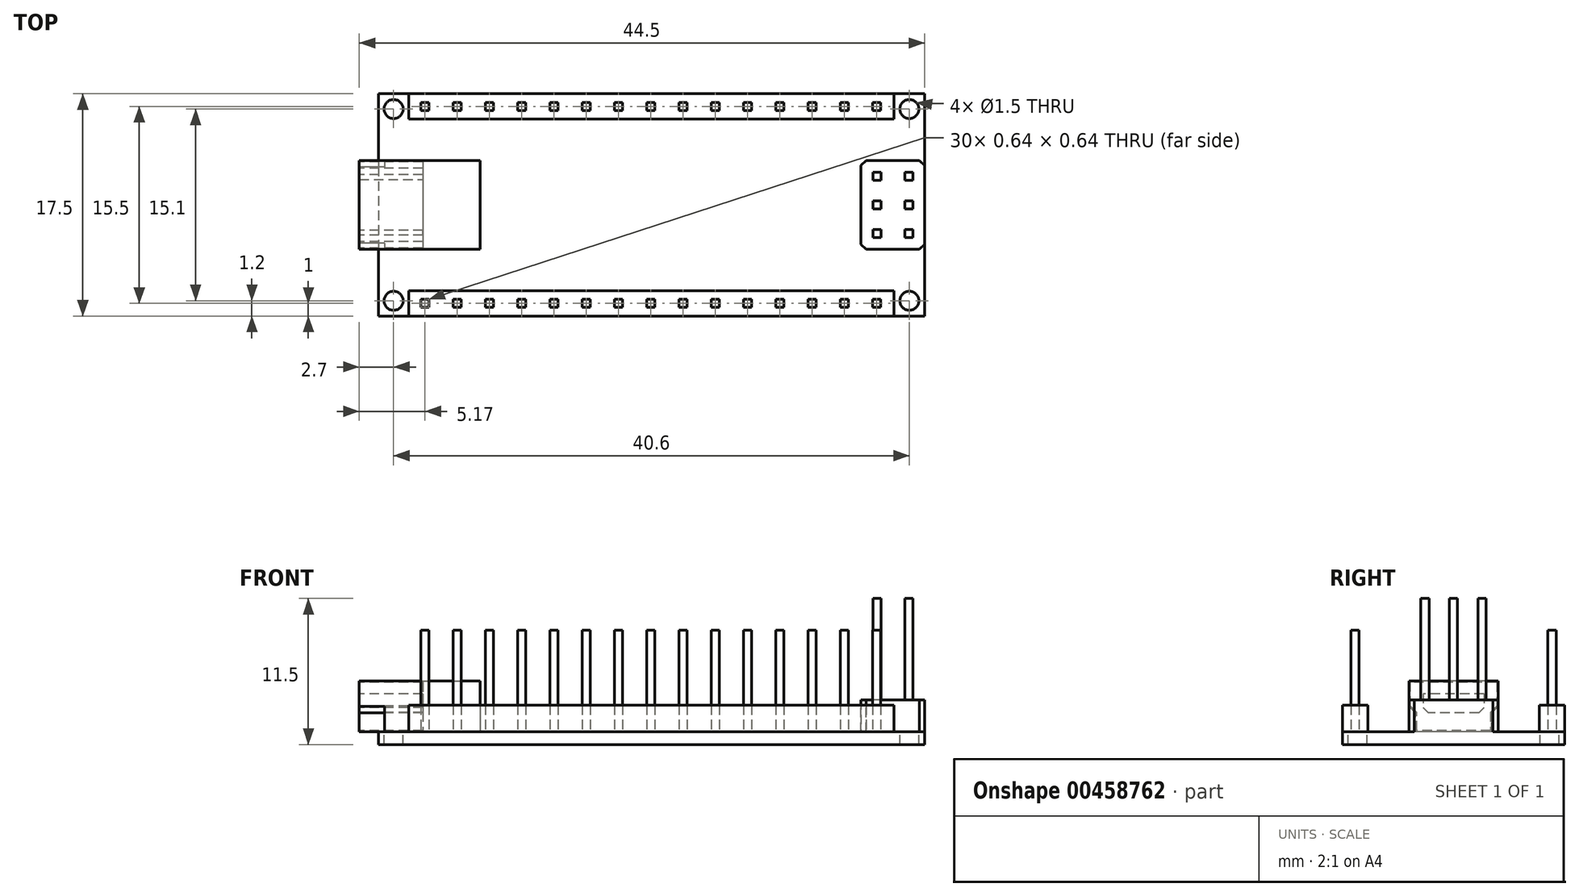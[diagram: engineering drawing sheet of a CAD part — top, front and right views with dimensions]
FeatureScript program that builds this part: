
annotation { "Feature Type Name" : "Feature", "Feature Type Description" : "" }
export const myFeature = defineFeature(function(context is Context, id is Id, definition is map)
    precondition{}
    {
        {
            var Q0;
            Q0=qCreatedBy(makeId("Top.planeOp"),FACE);
            var sketch = newSketch(context, id + "F0", { "sketchPlane" : qUnion([Q0])});
            skLineSegment(sketch, "E0.bottom", {"start": v(21.5, 8.75) * mm, "end": v(-21.5, 8.75) * mm});
            skLineSegment(sketch, "E0.top", {"start": v(21.5, -8.75) * mm, "end": v(-21.5, -8.75) * mm});
            skLineSegment(sketch, "E0.left", {"start": v(21.5, 8.75) * mm, "end": v(21.5, -8.75) * mm});
            skLineSegment(sketch, "E0.right", {"start": v(-21.5, 8.75) * mm, "end": v(-21.5, -8.75) * mm});
            skPoint(sketch, "E0.middle", {"position": v(0, 0) * mm});
            skCircle(sketch, "E1", {"center": v(-20.3, 7.55) * mm, "radius": 0.75 * mm});
            skCircle(sketch, "E2.0.1.0", {"center": v(-20.3, -7.55) * mm, "radius": 0.75 * mm});
            skCircle(sketch, "E2.1.0.0", {"center": v(20.3, 7.55) * mm, "radius": 0.75 * mm});
            skCircle(sketch, "E2.1.1.0", {"center": v(20.3, -7.55) * mm, "radius": 0.75 * mm});
            skLineSegment(sketch, "E2.direction1", {"start": v(-20.3, 7.55) * mm, "end": v(20.3, 7.55) * mm, "construction": true});
            skLineSegment(sketch, "E2.direction2", {"start": v(-20.3, 7.55) * mm, "end": v(-20.3, -7.55) * mm, "construction": true});
            skPoint(sketch, "E3", {"position": v(21.5, 0) * mm});
            skPoint(sketch, "E4", {"position": v(-21.5, 0) * mm});
            skLineSegment(sketch, "E5.bottom", {"start": v(-23, 3.5) * mm, "end": v(-13.5, 3.5) * mm});
            skLineSegment(sketch, "E5.top", {"start": v(-23, -3.5) * mm, "end": v(-13.5, -3.5) * mm});
            skLineSegment(sketch, "E5.left", {"start": v(-23, 3.5) * mm, "end": v(-23, -3.5) * mm});
            skLineSegment(sketch, "E5.right", {"start": v(-13.5, 3.5) * mm, "end": v(-13.5, -3.5) * mm});
            skPoint(sketch, "E6", {"position": v(-13.5, 0) * mm});
            skLineSegment(sketch, "E7.bottom", {"start": v(21.5, 3.5) * mm, "end": v(16.5, 3.5) * mm});
            skLineSegment(sketch, "E7.top", {"start": v(21.5, -3.5) * mm, "end": v(16.5, -3.5) * mm});
            skLineSegment(sketch, "E7.left", {"start": v(21.5, 3.5) * mm, "end": v(21.5, -3.5) * mm});
            skLineSegment(sketch, "E7.right", {"start": v(16.5, 3.5) * mm, "end": v(16.5, -3.5) * mm});
            skSolve(sketch);
        }
        {
            var Q0;
            {var subQ5=sQuery(id+"F0.wireOp",EDGE,"E5.right");Q0=makeQuery(id+"F0.imprint","IMPRINT",FACE,{"disambiguationData":[TD([[makeQuery(id+"F0.imprint","IMPRINT",EDGE,{"derivedFrom":subQ5}),-1.0]])]});}
            var Q1;
            {var subQ0=sQuery(id+"F0.wireOp",EDGE,"E0.bottom");Q1=makeQuery(id+"F0.imprint","IMPRINT",FACE,{"disambiguationData":[TD([[makeQuery(id+"F0.imprint","IMPRINT",EDGE,{"derivedFrom":subQ0}),1.0]])]});}
            var Q2;
            Q2=makeQuery(id+"F0.imprint","IMPRINT",FACE,{"disambiguationData":[TD([[makeQuery(id+"F0.imprint","IMPRINT",EDGE,{"derivedFrom":sQuery(id+"F0.wireOp",EDGE,"E7.bottom")}),1.0]])]});
            extrude(context, id + "F1", {"entities" : qUnion([Q0, Q1, Q2]), "oppositeDirection" : true, "depth" : 1 * mm});
        }
        {
            var Q0;
            {var subQ5=sQuery(id+"F0.wireOp",EDGE,"E5.left");Q0=makeQuery(id+"F0.imprint","IMPRINT",FACE,{"disambiguationData":[TD([[makeQuery(id+"F0.imprint","IMPRINT",EDGE,{"derivedFrom":subQ5}),1.0]])]});}
            var Q1;
            {var subQ5=sQuery(id+"F0.wireOp",EDGE,"E5.right");Q1=makeQuery(id+"F0.imprint","IMPRINT",FACE,{"disambiguationData":[TD([[makeQuery(id+"F0.imprint","IMPRINT",EDGE,{"derivedFrom":subQ5}),-1.0]])]});}
            extrude(context, id + "F2", {"entities" : qUnion([Q0, Q1]), "operationType" : NewBodyOperationType.ADD, "depth" : 4 * mm});
        }
        {
            var Q0;
            Q0=makeQuery(id+"F0.imprint","IMPRINT",FACE,{"disambiguationData":[TD([[makeQuery(id+"F0.imprint","IMPRINT",EDGE,{"derivedFrom":sQuery(id+"F0.wireOp",EDGE,"E7.bottom")}),1.0]])]});
            extrude(context, id + "F3", {"entities" : qUnion([Q0]), "operationType" : NewBodyOperationType.ADD, "depth" : 2.5 * mm});
        }
        {
            var Q0;
            Q0=makeQuery(id+"F2.opExtrude","SWEPT_FACE",FACE,{"disambiguationData":[OSD([sQuery(id+"F0.wireOp",EDGE,"E5.left")])]});
            var sketch = newSketch(context, id + "F4", { "sketchPlane" : qUnion([Q0])});
            skPoint(sketch, "E8", {"position": v(-3.5, 2) * mm});
            skPoint(sketch, "E9", {"position": v(3.5, 2) * mm});
            skPoint(sketch, "E10", {"position": v(-3, 0) * mm});
            skPoint(sketch, "E11", {"position": v(3, 0) * mm});
            skPoint(sketch, "E12", {"position": v(-3, 1.5) * mm});
            skPoint(sketch, "E13", {"position": v(3, 1.5) * mm});
            skLineSegment(sketch, "E14", {"start": v(-3.5, 2) * mm, "end": v(-3, 1.5) * mm});
            skLineSegment(sketch, "E15", {"start": v(-3, 0) * mm, "end": v(-3, 1.5) * mm});
            skLineSegment(sketch, "E16", {"start": v(3, 0) * mm, "end": v(3, 1.5) * mm});
            skLineSegment(sketch, "E17", {"start": v(3, 1.5) * mm, "end": v(3.5, 2) * mm});
            skLineSegment(sketch, "E18.bottom", {"start": v(-2.4, 3) * mm, "end": v(2.4, 3) * mm});
            skLineSegment(sketch, "E18.top", {"start": v(-2.4, 1.5) * mm, "end": v(2.4, 1.5) * mm});
            skLineSegment(sketch, "E18.left", {"start": v(-2.4, 3) * mm, "end": v(-2.4, 1.5) * mm});
            skLineSegment(sketch, "E18.right", {"start": v(2.4, 3) * mm, "end": v(2.4, 1.5) * mm});
            skPoint(sketch, "E19", {"position": v(0, 3) * mm});
            skPoint(sketch, "E20", {"position": v(-2.4, 2.25) * mm});
            skPoint(sketch, "E21", {"position": v(-3.5, 4) * mm});
            skPoint(sketch, "E22", {"position": v(3.5, 4) * mm});
            skLineSegment(sketch, "E23.0", {"start": v(-3.5, -1) * mm, "end": v(3.5, -1) * mm});
            skLineSegment(sketch, "E24", {"start": v(-3.5, 4) * mm, "end": v(-3.5, 2) * mm});
            skLineSegment(sketch, "E25", {"start": v(-3, 1.5) * mm, "end": v(-3, 0) * mm});
            skLineSegment(sketch, "E26", {"start": v(-3, 0) * mm, "end": v(3, 0) * mm});
            skLineSegment(sketch, "E27", {"start": v(3.5, 2) * mm, "end": v(3.5, 4) * mm});
            skLineSegment(sketch, "E28.0", {"start": v(-3.4, 3.9) * mm, "end": v(3.4, 3.9) * mm});
            skLineSegment(sketch, "E28.1", {"start": v(3.4, 2.04) * mm, "end": v(3.4, 3.9) * mm});
            skLineSegment(sketch, "E28.2", {"start": v(-3.4, 3.9) * mm, "end": v(-3.4, 2.04) * mm});
            skLineSegment(sketch, "E28.3", {"start": v(2.9, 1.54) * mm, "end": v(3.4, 2.04) * mm});
            skLineSegment(sketch, "E28.4", {"start": v(-3.4, 2.04) * mm, "end": v(-2.9, 1.54) * mm});
            skLineSegment(sketch, "E28.5", {"start": v(-2.9, 1.54) * mm, "end": v(-2.9, 0.1) * mm});
            skLineSegment(sketch, "E28.6", {"start": v(-2.9, 0.1) * mm, "end": v(2.9, 0.1) * mm});
            skLineSegment(sketch, "E28.7", {"start": v(2.9, 0.1) * mm, "end": v(2.9, 1.54) * mm});
            skPoint(sketch, "E29", {"position": v(-3.4, 2.04) * mm});
            skPoint(sketch, "E30", {"position": v(-2.9, 1.54) * mm});
            skSolve(sketch);
        }
        {
            var Q0;
            Q0=makeQuery(id+"F4.imprint","IMPRINT",FACE,{"disambiguationData":[TD([[makeQuery(id+"F4.imprint","IMPRINT",EDGE,{"derivedFrom":sQuery(id+"F4.wireOp",EDGE,"E18.bottom")}),1.0]])]});
            extrude(context, id + "F5", {"entities" : qUnion([Q0]), "operationType" : NewBodyOperationType.REMOVE, "oppositeDirection" : true, "depth" : 5 * mm});
        }
        {
            var Q0;
            {var subQ0=sQuery(id+"F4.wireOp",EDGE,"E14");Q0=makeQuery(id+"F4.imprint","IMPRINT",FACE,{"disambiguationData":[TD([[makeQuery(id+"F4.imprint","IMPRINT",EDGE,{"derivedFrom":subQ0}),-1.0]])]});}
            var Q1;
            {var subQ0=sQuery(id+"F4.wireOp",EDGE,"E16");Q1=makeQuery(id+"F4.imprint","IMPRINT",FACE,{"disambiguationData":[TD([[makeQuery(id+"F4.imprint","IMPRINT",EDGE,{"derivedFrom":subQ0}),-1.0]])]});}
            extrude(context, id + "F6", {"entities" : qUnion([Q0, Q1]), "operationType" : NewBodyOperationType.REMOVE, "oppositeDirection" : true, "depth" : 2 * mm});
        }
        {
            var Q0;
            Q0=makeQuery(id+"F1.opExtrude","CAP_FACE",FACE,{"disambiguationData":[OSD([sQuery(id+"F0.wireOp",EDGE,"E0.bottom"),sQuery(id+"F0.wireOp",EDGE,"E0.top"),sQuery(id+"F0.wireOp",EDGE,"E0.left"),sQuery(id+"F0.wireOp",EDGE,"E0.right"),sQuery(id+"F0.wireOp",EDGE,"E1"),sQuery(id+"F0.wireOp",EDGE,"E2.0.1.0"),sQuery(id+"F0.wireOp",EDGE,"E2.1.0.0"),sQuery(id+"F0.wireOp",EDGE,"E2.1.1.0"),sQuery(id+"F0.wireOp",EDGE,"E7.left")])],"isStart":false});
            var sketch = newSketch(context, id + "F7", { "sketchPlane" : qUnion([Q0])});
            skLineSegment(sketch, "E31.bottom", {"start": v(-19.1, 8.75) * mm, "end": v(19.1, 8.75) * mm});
            skLineSegment(sketch, "E31.top", {"start": v(-19.1, 6.75) * mm, "end": v(19.1, 6.75) * mm});
            skLineSegment(sketch, "E31.left", {"start": v(-19.1, 8.75) * mm, "end": v(-19.1, 6.75) * mm});
            skLineSegment(sketch, "E31.right", {"start": v(19.1, 8.75) * mm, "end": v(19.1, 6.75) * mm});
            skPoint(sketch, "E32", {"position": v(0, 6.75) * mm});
            skLineSegment(sketch, "E33", {"start": v(-19.1, 7.75) * mm, "end": v(19.1, 7.75) * mm, "construction": true});
            skPoint(sketch, "E34", {"position": v(-17.83, 7.75) * mm});
            skLineSegment(sketch, "E35.bottom", {"start": v(-17.51, 8.07) * mm, "end": v(-18.15, 8.07) * mm});
            skLineSegment(sketch, "E35.top", {"start": v(-17.51, 7.43) * mm, "end": v(-18.15, 7.43) * mm});
            skLineSegment(sketch, "E35.left", {"start": v(-17.51, 8.07) * mm, "end": v(-17.51, 7.43) * mm});
            skLineSegment(sketch, "E35.right", {"start": v(-18.15, 8.07) * mm, "end": v(-18.15, 7.43) * mm});
            skPoint(sketch, "E36.1.0.0", {"position": v(-15.3, 7.75) * mm});
            skLineSegment(sketch, "E36.1.0.1", {"start": v(-14.97, 8.07) * mm, "end": v(-14.97, 7.43) * mm});
            skLineSegment(sketch, "E36.1.0.2", {"start": v(-14.97, 8.07) * mm, "end": v(-15.61, 8.07) * mm});
            skLineSegment(sketch, "E36.1.0.3", {"start": v(-15.61, 8.07) * mm, "end": v(-15.61, 7.43) * mm});
            skLineSegment(sketch, "E36.1.0.4", {"start": v(-14.97, 7.43) * mm, "end": v(-15.61, 7.43) * mm});
            skPoint(sketch, "E36.2.0.0", {"position": v(-12.75, 7.75) * mm});
            skLineSegment(sketch, "E36.2.0.1", {"start": v(-12.43, 8.07) * mm, "end": v(-12.43, 7.43) * mm});
            skLineSegment(sketch, "E36.2.0.2", {"start": v(-12.43, 8.07) * mm, "end": v(-13.07, 8.07) * mm});
            skLineSegment(sketch, "E36.2.0.3", {"start": v(-13.07, 8.07) * mm, "end": v(-13.07, 7.43) * mm});
            skLineSegment(sketch, "E36.2.0.4", {"start": v(-12.43, 7.43) * mm, "end": v(-13.07, 7.43) * mm});
            skPoint(sketch, "E36.3.0.0", {"position": v(-10.21, 7.75) * mm});
            skLineSegment(sketch, "E36.3.0.1", {"start": v(-9.89, 8.07) * mm, "end": v(-9.89, 7.43) * mm});
            skLineSegment(sketch, "E36.3.0.2", {"start": v(-9.89, 8.07) * mm, "end": v(-10.53, 8.07) * mm});
            skLineSegment(sketch, "E36.3.0.3", {"start": v(-10.53, 8.07) * mm, "end": v(-10.53, 7.43) * mm});
            skLineSegment(sketch, "E36.3.0.4", {"start": v(-9.89, 7.43) * mm, "end": v(-10.53, 7.43) * mm});
            skPoint(sketch, "E36.4.0.0", {"position": v(-7.67, 7.75) * mm});
            skLineSegment(sketch, "E36.4.0.1", {"start": v(-7.35, 8.07) * mm, "end": v(-7.35, 7.43) * mm});
            skLineSegment(sketch, "E36.4.0.2", {"start": v(-7.35, 8.07) * mm, "end": v(-8, 8.07) * mm});
            skLineSegment(sketch, "E36.4.0.3", {"start": v(-8, 8.07) * mm, "end": v(-8, 7.43) * mm});
            skLineSegment(sketch, "E36.4.0.4", {"start": v(-7.35, 7.43) * mm, "end": v(-8, 7.43) * mm});
            skPoint(sketch, "E36.5.0.0", {"position": v(-5.13, 7.75) * mm});
            skLineSegment(sketch, "E36.5.0.1", {"start": v(-4.8, 8.07) * mm, "end": v(-4.8, 7.43) * mm});
            skLineSegment(sketch, "E36.5.0.2", {"start": v(-4.8, 8.07) * mm, "end": v(-5.45, 8.07) * mm});
            skLineSegment(sketch, "E36.5.0.3", {"start": v(-5.45, 8.07) * mm, "end": v(-5.45, 7.43) * mm});
            skLineSegment(sketch, "E36.5.0.4", {"start": v(-4.8, 7.43) * mm, "end": v(-5.45, 7.43) * mm});
            skPoint(sketch, "E36.6.0.0", {"position": v(-2.59, 7.75) * mm});
            skLineSegment(sketch, "E36.6.0.1", {"start": v(-2.27, 8.07) * mm, "end": v(-2.27, 7.43) * mm});
            skLineSegment(sketch, "E36.6.0.2", {"start": v(-2.27, 8.07) * mm, "end": v(-2.9, 8.07) * mm});
            skLineSegment(sketch, "E36.6.0.3", {"start": v(-2.9, 8.07) * mm, "end": v(-2.9, 7.43) * mm});
            skLineSegment(sketch, "E36.6.0.4", {"start": v(-2.27, 7.43) * mm, "end": v(-2.9, 7.43) * mm});
            skPoint(sketch, "E36.7.0.0", {"position": v(-0.05, 7.75) * mm});
            skLineSegment(sketch, "E36.7.0.1", {"start": v(0.27, 8.07) * mm, "end": v(0.27, 7.43) * mm});
            skLineSegment(sketch, "E36.7.0.2", {"start": v(0.27, 8.07) * mm, "end": v(-0.37, 8.07) * mm});
            skLineSegment(sketch, "E36.7.0.3", {"start": v(-0.37, 8.07) * mm, "end": v(-0.37, 7.43) * mm});
            skLineSegment(sketch, "E36.7.0.4", {"start": v(0.27, 7.43) * mm, "end": v(-0.37, 7.43) * mm});
            skPoint(sketch, "E36.8.0.0", {"position": v(2.5, 7.75) * mm});
            skLineSegment(sketch, "E36.8.0.1", {"start": v(2.81, 8.07) * mm, "end": v(2.81, 7.43) * mm});
            skLineSegment(sketch, "E36.8.0.2", {"start": v(2.81, 8.07) * mm, "end": v(2.17, 8.07) * mm});
            skLineSegment(sketch, "E36.8.0.3", {"start": v(2.17, 8.07) * mm, "end": v(2.17, 7.43) * mm});
            skLineSegment(sketch, "E36.8.0.4", {"start": v(2.81, 7.43) * mm, "end": v(2.17, 7.43) * mm});
            skPoint(sketch, "E36.9.0.0", {"position": v(5.03, 7.75) * mm});
            skLineSegment(sketch, "E36.9.0.1", {"start": v(5.35, 8.07) * mm, "end": v(5.35, 7.43) * mm});
            skLineSegment(sketch, "E36.9.0.2", {"start": v(5.35, 8.07) * mm, "end": v(4.71, 8.07) * mm});
            skLineSegment(sketch, "E36.9.0.3", {"start": v(4.71, 8.07) * mm, "end": v(4.71, 7.43) * mm});
            skLineSegment(sketch, "E36.9.0.4", {"start": v(5.35, 7.43) * mm, "end": v(4.71, 7.43) * mm});
            skPoint(sketch, "E36.10.0.0", {"position": v(7.57, 7.75) * mm});
            skLineSegment(sketch, "E36.10.0.1", {"start": v(7.9, 8.07) * mm, "end": v(7.9, 7.43) * mm});
            skLineSegment(sketch, "E36.10.0.2", {"start": v(7.9, 8.07) * mm, "end": v(7.25, 8.07) * mm});
            skLineSegment(sketch, "E36.10.0.3", {"start": v(7.25, 8.07) * mm, "end": v(7.25, 7.43) * mm});
            skLineSegment(sketch, "E36.10.0.4", {"start": v(7.9, 7.43) * mm, "end": v(7.25, 7.43) * mm});
            skPoint(sketch, "E36.11.0.0", {"position": v(10.11, 7.75) * mm});
            skLineSegment(sketch, "E36.11.0.1", {"start": v(10.43, 8.07) * mm, "end": v(10.43, 7.43) * mm});
            skLineSegment(sketch, "E36.11.0.2", {"start": v(10.43, 8.07) * mm, "end": v(9.8, 8.07) * mm});
            skLineSegment(sketch, "E36.11.0.3", {"start": v(9.8, 8.07) * mm, "end": v(9.8, 7.43) * mm});
            skLineSegment(sketch, "E36.11.0.4", {"start": v(10.43, 7.43) * mm, "end": v(9.8, 7.43) * mm});
            skPoint(sketch, "E36.12.0.0", {"position": v(12.65, 7.75) * mm});
            skLineSegment(sketch, "E36.12.0.1", {"start": v(12.97, 8.07) * mm, "end": v(12.97, 7.43) * mm});
            skLineSegment(sketch, "E36.12.0.2", {"start": v(12.97, 8.07) * mm, "end": v(12.33, 8.07) * mm});
            skLineSegment(sketch, "E36.12.0.3", {"start": v(12.33, 8.07) * mm, "end": v(12.33, 7.43) * mm});
            skLineSegment(sketch, "E36.12.0.4", {"start": v(12.97, 7.43) * mm, "end": v(12.33, 7.43) * mm});
            skPoint(sketch, "E36.13.0.0", {"position": v(15.2, 7.75) * mm});
            skLineSegment(sketch, "E36.13.0.1", {"start": v(15.51, 8.07) * mm, "end": v(15.51, 7.43) * mm});
            skLineSegment(sketch, "E36.13.0.2", {"start": v(15.51, 8.07) * mm, "end": v(14.87, 8.07) * mm});
            skLineSegment(sketch, "E36.13.0.3", {"start": v(14.87, 8.07) * mm, "end": v(14.87, 7.43) * mm});
            skLineSegment(sketch, "E36.13.0.4", {"start": v(15.51, 7.43) * mm, "end": v(14.87, 7.43) * mm});
            skPoint(sketch, "E36.14.0.0", {"position": v(17.73, 7.75) * mm});
            skLineSegment(sketch, "E36.14.0.1", {"start": v(18.05, 8.07) * mm, "end": v(18.05, 7.43) * mm});
            skLineSegment(sketch, "E36.14.0.2", {"start": v(18.05, 8.07) * mm, "end": v(17.41, 8.07) * mm});
            skLineSegment(sketch, "E36.14.0.3", {"start": v(17.41, 8.07) * mm, "end": v(17.41, 7.43) * mm});
            skLineSegment(sketch, "E36.14.0.4", {"start": v(18.05, 7.43) * mm, "end": v(17.41, 7.43) * mm});
            skLineSegment(sketch, "E36.direction1", {"start": v(-17.83, 7.75) * mm, "end": v(-15.3, 7.75) * mm, "construction": true});
            skPoint(sketch, "E37", {"position": v(-20.3, 7.55) * mm});
            skLineSegment(sketch, "E38", {"start": v(-20.3, 7.55) * mm, "end": v(-21.5, 7.55) * mm});
            skLineSegment(sketch, "E39", {"start": v(-21.5, 7.55) * mm, "end": v(-19.1, 7.55) * mm});
            skPoint(sketch, "E40", {"position": v(-21.05, 7.55) * mm});
            skPoint(sketch, "E41", {"position": v(-19.55, 7.55) * mm});
            skPoint(sketch, "E42", {"position": v(20.3, 7.55) * mm});
            skLineSegment(sketch, "E43", {"start": v(20.3, 7.55) * mm, "end": v(21.5, 7.55) * mm});
            skLineSegment(sketch, "E44", {"start": v(21.5, 7.55) * mm, "end": v(19.1, 7.55) * mm});
            skPoint(sketch, "E45", {"position": v(21.05, 7.55) * mm});
            skPoint(sketch, "E46", {"position": v(19.55, 7.55) * mm});
            skPoint(sketch, "E47.0.1.0", {"position": v(-0.05, -7.75) * mm});
            skPoint(sketch, "E47.0.1.1", {"position": v(-5.13, -7.75) * mm});
            skPoint(sketch, "E47.0.1.2", {"position": v(12.65, -7.75) * mm});
            skPoint(sketch, "E47.0.1.3", {"position": v(-7.67, -7.75) * mm});
            skPoint(sketch, "E47.0.1.4", {"position": v(17.73, -7.75) * mm});
            skPoint(sketch, "E47.0.1.5", {"position": v(-10.21, -7.75) * mm});
            skPoint(sketch, "E47.0.1.6", {"position": v(7.57, -7.75) * mm});
            skPoint(sketch, "E47.0.1.7", {"position": v(2.49, -7.75) * mm});
            skPoint(sketch, "E47.0.1.8", {"position": v(0, -8.75) * mm});
            skPoint(sketch, "E47.0.1.9", {"position": v(-17.83, -7.75) * mm});
            skPoint(sketch, "E47.0.1.10", {"position": v(5.03, -7.75) * mm});
            skPoint(sketch, "E47.0.1.11", {"position": v(-15.3, -7.75) * mm});
            skLineSegment(sketch, "E47.0.1.12", {"start": v(-17.83, -7.75) * mm, "end": v(-15.3, -7.75) * mm, "construction": true});
            skPoint(sketch, "E47.0.1.13", {"position": v(10.11, -7.75) * mm});
            skPoint(sketch, "E47.0.1.14", {"position": v(15.2, -7.75) * mm});
            skPoint(sketch, "E47.0.1.15", {"position": v(-2.6, -7.75) * mm});
            skPoint(sketch, "E47.0.1.16", {"position": v(-12.75, -7.75) * mm});
            skPoint(sketch, "E47.0.1.17", {"position": v(-17.83, -7.75) * mm});
            skLineSegment(sketch, "E47.0.1.18", {"start": v(18.05, -7.43) * mm, "end": v(17.41, -7.43) * mm});
            skLineSegment(sketch, "E47.0.1.19", {"start": v(18.05, -8.07) * mm, "end": v(17.41, -8.07) * mm});
            skLineSegment(sketch, "E47.0.1.20", {"start": v(18.05, -7.43) * mm, "end": v(18.05, -8.07) * mm});
            skLineSegment(sketch, "E47.0.1.21", {"start": v(-0.37, -7.43) * mm, "end": v(-0.37, -8.07) * mm});
            skLineSegment(sketch, "E47.0.1.22", {"start": v(-10.53, -7.43) * mm, "end": v(-10.53, -8.07) * mm});
            skLineSegment(sketch, "E47.0.1.23", {"start": v(-9.89, -7.43) * mm, "end": v(-10.53, -7.43) * mm});
            skLineSegment(sketch, "E47.0.1.24", {"start": v(-2.27, -7.43) * mm, "end": v(-2.9, -7.43) * mm});
            skLineSegment(sketch, "E47.0.1.25", {"start": v(12.97, -7.43) * mm, "end": v(12.97, -8.07) * mm});
            skLineSegment(sketch, "E47.0.1.26", {"start": v(-5.45, -7.43) * mm, "end": v(-5.45, -8.07) * mm});
            skLineSegment(sketch, "E47.0.1.27", {"start": v(-7.35, -8.07) * mm, "end": v(-7.99, -8.07) * mm});
            skLineSegment(sketch, "E47.0.1.28", {"start": v(2.81, -8.07) * mm, "end": v(2.17, -8.07) * mm});
            skLineSegment(sketch, "E47.0.1.29", {"start": v(12.97, -8.07) * mm, "end": v(12.33, -8.07) * mm});
            skLineSegment(sketch, "E47.0.1.30", {"start": v(7.9, -8.07) * mm, "end": v(7.25, -8.07) * mm});
            skLineSegment(sketch, "E47.0.1.31", {"start": v(7.25, -7.43) * mm, "end": v(7.25, -8.07) * mm});
            skLineSegment(sketch, "E47.0.1.32", {"start": v(-2.9, -7.43) * mm, "end": v(-2.9, -8.07) * mm});
            skLineSegment(sketch, "E47.0.1.33", {"start": v(-7.35, -7.43) * mm, "end": v(-7.99, -7.43) * mm});
            skLineSegment(sketch, "E47.0.1.34", {"start": v(2.81, -7.43) * mm, "end": v(2.81, -8.07) * mm});
            skLineSegment(sketch, "E47.0.1.35", {"start": v(7.9, -7.43) * mm, "end": v(7.25, -7.43) * mm});
            skLineSegment(sketch, "E47.0.1.36", {"start": v(-4.8, -8.07) * mm, "end": v(-5.45, -8.07) * mm});
            skLineSegment(sketch, "E47.0.1.37", {"start": v(-7.35, -7.43) * mm, "end": v(-7.35, -8.07) * mm});
            skLineSegment(sketch, "E47.0.1.38", {"start": v(15.5, -8.07) * mm, "end": v(14.87, -8.07) * mm});
            skLineSegment(sketch, "E47.0.1.39", {"start": v(5.35, -8.07) * mm, "end": v(4.71, -8.07) * mm});
            skLineSegment(sketch, "E47.0.1.40", {"start": v(-2.27, -8.07) * mm, "end": v(-2.9, -8.07) * mm});
            skLineSegment(sketch, "E47.0.1.41", {"start": v(-12.43, -8.07) * mm, "end": v(-13.07, -8.07) * mm});
            skLineSegment(sketch, "E47.0.1.42", {"start": v(2.81, -7.43) * mm, "end": v(2.17, -7.43) * mm});
            skLineSegment(sketch, "E47.0.1.43", {"start": v(17.41, -7.43) * mm, "end": v(17.41, -8.07) * mm});
            skLineSegment(sketch, "E47.0.1.44", {"start": v(12.97, -7.43) * mm, "end": v(12.33, -7.43) * mm});
            skLineSegment(sketch, "E47.0.1.45", {"start": v(7.9, -7.43) * mm, "end": v(7.9, -8.07) * mm});
            skLineSegment(sketch, "E47.0.1.46", {"start": v(-2.27, -7.43) * mm, "end": v(-2.27, -8.07) * mm});
            skLineSegment(sketch, "E47.0.1.47", {"start": v(-17.5, -8.07) * mm, "end": v(-18.15, -8.07) * mm});
            skLineSegment(sketch, "E47.0.1.48", {"start": v(12.33, -7.43) * mm, "end": v(12.33, -8.07) * mm});
            skLineSegment(sketch, "E47.0.1.49", {"start": v(-14.97, -7.43) * mm, "end": v(-14.97, -8.07) * mm});
            skLineSegment(sketch, "E47.0.1.50", {"start": v(2.17, -7.43) * mm, "end": v(2.17, -8.07) * mm});
            skLineSegment(sketch, "E47.0.1.51", {"start": v(-8, -7.43) * mm, "end": v(-8, -8.07) * mm});
            skLineSegment(sketch, "E47.0.1.52", {"start": v(-14.97, -7.43) * mm, "end": v(-15.6, -7.43) * mm});
            skLineSegment(sketch, "E47.0.1.53", {"start": v(-15.61, -7.43) * mm, "end": v(-15.61, -8.07) * mm});
            skLineSegment(sketch, "E47.0.1.54", {"start": v(-14.97, -8.07) * mm, "end": v(-15.6, -8.07) * mm});
            skLineSegment(sketch, "E47.0.1.55", {"start": v(-9.89, -7.43) * mm, "end": v(-9.89, -8.07) * mm});
            skLineSegment(sketch, "E47.0.1.56", {"start": v(0.27, -7.43) * mm, "end": v(0.27, -8.07) * mm});
            skLineSegment(sketch, "E47.0.1.57", {"start": v(10.43, -7.43) * mm, "end": v(10.43, -8.07) * mm});
            skLineSegment(sketch, "E47.0.1.58", {"start": v(-12.43, -7.43) * mm, "end": v(-12.43, -8.07) * mm});
            skLineSegment(sketch, "E47.0.1.59", {"start": v(10.43, -7.43) * mm, "end": v(9.8, -7.43) * mm});
            skLineSegment(sketch, "E47.0.1.60", {"start": v(0.27, -7.43) * mm, "end": v(-0.37, -7.43) * mm});
            skLineSegment(sketch, "E47.0.1.61", {"start": v(15.51, -7.43) * mm, "end": v(15.51, -8.07) * mm});
            skLineSegment(sketch, "E47.0.1.62", {"start": v(5.35, -7.43) * mm, "end": v(5.35, -8.07) * mm});
            skLineSegment(sketch, "E47.0.1.63", {"start": v(-4.8, -7.43) * mm, "end": v(-4.8, -8.07) * mm});
            skLineSegment(sketch, "E47.0.1.64", {"start": v(15.51, -7.43) * mm, "end": v(14.87, -7.43) * mm});
            skLineSegment(sketch, "E47.0.1.65", {"start": v(5.35, -7.43) * mm, "end": v(4.71, -7.43) * mm});
            skLineSegment(sketch, "E47.0.1.66", {"start": v(-4.8, -7.43) * mm, "end": v(-5.45, -7.43) * mm});
            skLineSegment(sketch, "E47.0.1.67", {"start": v(10.43, -8.07) * mm, "end": v(9.8, -8.07) * mm});
            skLineSegment(sketch, "E47.0.1.68", {"start": v(0.27, -8.07) * mm, "end": v(-0.37, -8.07) * mm});
            skLineSegment(sketch, "E47.0.1.69", {"start": v(-9.9, -8.07) * mm, "end": v(-10.53, -8.07) * mm});
            skLineSegment(sketch, "E47.0.1.70", {"start": v(4.71, -7.43) * mm, "end": v(4.71, -8.07) * mm});
            skLineSegment(sketch, "E47.0.1.71", {"start": v(14.87, -7.43) * mm, "end": v(14.87, -8.07) * mm});
            skLineSegment(sketch, "E47.0.1.72", {"start": v(9.8, -7.43) * mm, "end": v(9.8, -8.07) * mm});
            skLineSegment(sketch, "E47.0.1.73", {"start": v(-12.43, -7.43) * mm, "end": v(-13.07, -7.43) * mm});
            skLineSegment(sketch, "E47.0.1.74", {"start": v(-13.07, -7.43) * mm, "end": v(-13.07, -8.07) * mm});
            skLineSegment(sketch, "E47.0.1.75", {"start": v(-18.15, -7.43) * mm, "end": v(-18.15, -8.07) * mm});
            skLineSegment(sketch, "E47.0.1.76", {"start": v(-17.51, -7.43) * mm, "end": v(-17.51, -8.07) * mm});
            skLineSegment(sketch, "E47.0.1.77", {"start": v(-17.5, -7.43) * mm, "end": v(-18.15, -7.43) * mm});
            skLineSegment(sketch, "E47.0.1.78", {"start": v(19.1, -6.75) * mm, "end": v(19.1, -8.75) * mm});
            skLineSegment(sketch, "E47.0.1.79", {"start": v(-19.1, -8.75) * mm, "end": v(19.1, -8.75) * mm});
            skLineSegment(sketch, "E47.0.1.80", {"start": v(-19.1, -6.75) * mm, "end": v(-19.1, -8.75) * mm});
            skLineSegment(sketch, "E47.0.1.81", {"start": v(-19.1, -6.75) * mm, "end": v(19.1, -6.75) * mm});
            skLineSegment(sketch, "E47.direction1", {"start": v(-0.05, 7.75) * mm, "end": v(24.95, 7.75) * mm, "construction": true});
            skLineSegment(sketch, "E47.direction2", {"start": v(-0.05, 7.75) * mm, "end": v(-0.05, -7.75) * mm, "construction": true});
            skSolve(sketch);
        }
        {
            var Q0;
            Q0=makeQuery(id+"F7.imprint","IMPRINT",FACE,{"disambiguationData":[TD([[makeQuery(id+"F7.imprint","IMPRINT",EDGE,{"derivedFrom":sQuery(id+"F7.wireOp",EDGE,"E47.0.1.18")}),-1.0]])]});
            var Q1;
            {var subQ1=sQuery(id+"F7.wireOp",EDGE,"E31.bottom");Q1=makeQuery(id+"F7.imprint","IMPRINT",FACE,{"disambiguationData":[TD([[makeQuery(id+"F7.imprint","IMPRINT",EDGE,{"derivedFrom":subQ1}),1.0]])]});}
            extrude(context, id + "F8", {"entities" : qUnion([Q0, Q1]), "depth" : 2.1 * mm});
        }
        {
            var Q0;
            Q0=makeQuery(id+"F7.imprint","IMPRINT",FACE,{"disambiguationData":[TD([[makeQuery(id+"F7.imprint","IMPRINT",EDGE,{"derivedFrom":sQuery(id+"F7.wireOp",EDGE,"E35.bottom")}),1.0]])]});
            var Q1;
            Q1=makeQuery(id+"F7.imprint","IMPRINT",FACE,{"disambiguationData":[TD([[makeQuery(id+"F7.imprint","IMPRINT",EDGE,{"derivedFrom":sQuery(id+"F7.wireOp",EDGE,"E36.1.0.1")}),-1.0]])]});
            var Q2;
            Q2=makeQuery(id+"F7.imprint","IMPRINT",FACE,{"disambiguationData":[TD([[makeQuery(id+"F7.imprint","IMPRINT",EDGE,{"derivedFrom":sQuery(id+"F7.wireOp",EDGE,"E36.2.0.1")}),-1.0]])]});
            var Q3;
            Q3=makeQuery(id+"F7.imprint","IMPRINT",FACE,{"disambiguationData":[TD([[makeQuery(id+"F7.imprint","IMPRINT",EDGE,{"derivedFrom":sQuery(id+"F7.wireOp",EDGE,"E36.3.0.1")}),-1.0]])]});
            var Q4;
            Q4=makeQuery(id+"F7.imprint","IMPRINT",FACE,{"disambiguationData":[TD([[makeQuery(id+"F7.imprint","IMPRINT",EDGE,{"derivedFrom":sQuery(id+"F7.wireOp",EDGE,"E36.4.0.1")}),-1.0]])]});
            var Q5;
            Q5=makeQuery(id+"F7.imprint","IMPRINT",FACE,{"disambiguationData":[TD([[makeQuery(id+"F7.imprint","IMPRINT",EDGE,{"derivedFrom":sQuery(id+"F7.wireOp",EDGE,"E36.5.0.1")}),-1.0]])]});
            var Q6;
            Q6=makeQuery(id+"F7.imprint","IMPRINT",FACE,{"disambiguationData":[TD([[makeQuery(id+"F7.imprint","IMPRINT",EDGE,{"derivedFrom":sQuery(id+"F7.wireOp",EDGE,"E36.6.0.1")}),-1.0]])]});
            var Q7;
            Q7=makeQuery(id+"F7.imprint","IMPRINT",FACE,{"disambiguationData":[TD([[makeQuery(id+"F7.imprint","IMPRINT",EDGE,{"derivedFrom":sQuery(id+"F7.wireOp",EDGE,"E36.7.0.1")}),-1.0]])]});
            var Q8;
            Q8=makeQuery(id+"F7.imprint","IMPRINT",FACE,{"disambiguationData":[TD([[makeQuery(id+"F7.imprint","IMPRINT",EDGE,{"derivedFrom":sQuery(id+"F7.wireOp",EDGE,"E36.8.0.1")}),-1.0]])]});
            var Q9;
            Q9=makeQuery(id+"F7.imprint","IMPRINT",FACE,{"disambiguationData":[TD([[makeQuery(id+"F7.imprint","IMPRINT",EDGE,{"derivedFrom":sQuery(id+"F7.wireOp",EDGE,"E36.9.0.1")}),-1.0]])]});
            var Q10;
            Q10=makeQuery(id+"F7.imprint","IMPRINT",FACE,{"disambiguationData":[TD([[makeQuery(id+"F7.imprint","IMPRINT",EDGE,{"derivedFrom":sQuery(id+"F7.wireOp",EDGE,"E36.10.0.1")}),-1.0]])]});
            var Q11;
            Q11=makeQuery(id+"F7.imprint","IMPRINT",FACE,{"disambiguationData":[TD([[makeQuery(id+"F7.imprint","IMPRINT",EDGE,{"derivedFrom":sQuery(id+"F7.wireOp",EDGE,"E36.11.0.1")}),-1.0]])]});
            var Q12;
            Q12=makeQuery(id+"F7.imprint","IMPRINT",FACE,{"disambiguationData":[TD([[makeQuery(id+"F7.imprint","IMPRINT",EDGE,{"derivedFrom":sQuery(id+"F7.wireOp",EDGE,"E36.12.0.1")}),-1.0]])]});
            var Q13;
            Q13=makeQuery(id+"F7.imprint","IMPRINT",FACE,{"disambiguationData":[TD([[makeQuery(id+"F7.imprint","IMPRINT",EDGE,{"derivedFrom":sQuery(id+"F7.wireOp",EDGE,"E36.13.0.1")}),-1.0]])]});
            var Q14;
            Q14=makeQuery(id+"F7.imprint","IMPRINT",FACE,{"disambiguationData":[TD([[makeQuery(id+"F7.imprint","IMPRINT",EDGE,{"derivedFrom":sQuery(id+"F7.wireOp",EDGE,"E36.14.0.1")}),-1.0]])]});
            var Q15;
            Q15=makeQuery(id+"F7.imprint","IMPRINT",FACE,{"disambiguationData":[TD([[makeQuery(id+"F7.imprint","IMPRINT",EDGE,{"derivedFrom":sQuery(id+"F7.wireOp",EDGE,"E47.0.1.47")}),-1.0]])]});
            var Q16;
            Q16=makeQuery(id+"F7.imprint","IMPRINT",FACE,{"disambiguationData":[TD([[makeQuery(id+"F7.imprint","IMPRINT",EDGE,{"derivedFrom":sQuery(id+"F7.wireOp",EDGE,"E47.0.1.49")}),-1.0]])]});
            var Q17;
            Q17=makeQuery(id+"F7.imprint","IMPRINT",FACE,{"disambiguationData":[TD([[makeQuery(id+"F7.imprint","IMPRINT",EDGE,{"derivedFrom":sQuery(id+"F7.wireOp",EDGE,"E47.0.1.41")}),-1.0]])]});
            var Q18;
            Q18=makeQuery(id+"F7.imprint","IMPRINT",FACE,{"disambiguationData":[TD([[makeQuery(id+"F7.imprint","IMPRINT",EDGE,{"derivedFrom":sQuery(id+"F7.wireOp",EDGE,"E47.0.1.22")}),1.0]])]});
            var Q19;
            Q19=makeQuery(id+"F7.imprint","IMPRINT",FACE,{"disambiguationData":[TD([[makeQuery(id+"F7.imprint","IMPRINT",EDGE,{"derivedFrom":sQuery(id+"F7.wireOp",EDGE,"E47.0.1.27")}),-1.0]])]});
            var Q20;
            Q20=makeQuery(id+"F7.imprint","IMPRINT",FACE,{"disambiguationData":[TD([[makeQuery(id+"F7.imprint","IMPRINT",EDGE,{"derivedFrom":sQuery(id+"F7.wireOp",EDGE,"E47.0.1.26")}),1.0]])]});
            var Q21;
            Q21=makeQuery(id+"F7.imprint","IMPRINT",FACE,{"disambiguationData":[TD([[makeQuery(id+"F7.imprint","IMPRINT",EDGE,{"derivedFrom":sQuery(id+"F7.wireOp",EDGE,"E47.0.1.24")}),1.0]])]});
            var Q22;
            Q22=makeQuery(id+"F7.imprint","IMPRINT",FACE,{"disambiguationData":[TD([[makeQuery(id+"F7.imprint","IMPRINT",EDGE,{"derivedFrom":sQuery(id+"F7.wireOp",EDGE,"E47.0.1.21")}),1.0]])]});
            var Q23;
            Q23=makeQuery(id+"F7.imprint","IMPRINT",FACE,{"disambiguationData":[TD([[makeQuery(id+"F7.imprint","IMPRINT",EDGE,{"derivedFrom":sQuery(id+"F7.wireOp",EDGE,"E47.0.1.28")}),-1.0]])]});
            var Q24;
            Q24=makeQuery(id+"F7.imprint","IMPRINT",FACE,{"disambiguationData":[TD([[makeQuery(id+"F7.imprint","IMPRINT",EDGE,{"derivedFrom":sQuery(id+"F7.wireOp",EDGE,"E47.0.1.39")}),-1.0]])]});
            var Q25;
            Q25=makeQuery(id+"F7.imprint","IMPRINT",FACE,{"disambiguationData":[TD([[makeQuery(id+"F7.imprint","IMPRINT",EDGE,{"derivedFrom":sQuery(id+"F7.wireOp",EDGE,"E47.0.1.30")}),-1.0]])]});
            var Q26;
            Q26=makeQuery(id+"F7.imprint","IMPRINT",FACE,{"disambiguationData":[TD([[makeQuery(id+"F7.imprint","IMPRINT",EDGE,{"derivedFrom":sQuery(id+"F7.wireOp",EDGE,"E47.0.1.57")}),-1.0]])]});
            var Q27;
            Q27=makeQuery(id+"F7.imprint","IMPRINT",FACE,{"disambiguationData":[TD([[makeQuery(id+"F7.imprint","IMPRINT",EDGE,{"derivedFrom":sQuery(id+"F7.wireOp",EDGE,"E47.0.1.25")}),-1.0]])]});
            var Q28;
            Q28=makeQuery(id+"F7.imprint","IMPRINT",FACE,{"disambiguationData":[TD([[makeQuery(id+"F7.imprint","IMPRINT",EDGE,{"derivedFrom":sQuery(id+"F7.wireOp",EDGE,"E47.0.1.38")}),-1.0]])]});
            var Q29;
            Q29=makeQuery(id+"F7.imprint","IMPRINT",FACE,{"disambiguationData":[TD([[makeQuery(id+"F7.imprint","IMPRINT",EDGE,{"derivedFrom":sQuery(id+"F7.wireOp",EDGE,"E47.0.1.18")}),1.0]])]});
            extrude(context, id + "F9", {"entities" : qUnion([Q0, Q1, Q2, Q3, Q4, Q5, Q6, Q7, Q8, Q9, Q10, Q11, Q12, Q13, Q14, Q15, Q16, Q17, Q18, Q19, Q20, Q21, Q22, Q23, Q24, Q25, Q26, Q27, Q28, Q29]), "depth" : 8 * mm, "offsetDistance" : 25 * mm});
        }
        {
            var Q0;
            Q0=makeQuery(id+"F5.boolean.opBoolean","COPY",EDGE,{"derivedFrom":makeQuery(id+"F5.opExtrude","SWEPT_EDGE",EDGE,{"disambiguationData":[OSD([sQuery(id+"F4.wireOp",EDGE,"E18.top"),sQuery(id+"F4.wireOp",EDGE,"E18.right")])]})});
            var Q1;
            Q1=makeQuery(id+"F5.boolean.opBoolean","COPY",EDGE,{"derivedFrom":makeQuery(id+"F5.opExtrude","SWEPT_EDGE",EDGE,{"disambiguationData":[OSD([sQuery(id+"F4.wireOp",EDGE,"E18.top"),sQuery(id+"F4.wireOp",EDGE,"E18.left")])]})});
            chamfer(context, id + "F10", {"entities" : qUnion([Q0, Q1]), "width" : 0.4 * mm, "tangentPropagation" : true});
        }
        {
            var Q0;
            Q0=makeQuery(id+"F3.opExtrude","CAP_FACE",FACE,{"disambiguationData":[OSD([sQuery(id+"F0.wireOp",EDGE,"E7.bottom"),sQuery(id+"F0.wireOp",EDGE,"E7.top"),sQuery(id+"F0.wireOp",EDGE,"E7.left"),sQuery(id+"F0.wireOp",EDGE,"E7.right")])],"isStart":false});
            var sketch = newSketch(context, id + "F11", { "sketchPlane" : qUnion([Q0])});
            skPoint(sketch, "E48", {"position": v(21.5, 1.17) * mm});
            skPoint(sketch, "E49", {"position": v(21.5, -1.17) * mm});
            skLineSegment(sketch, "E50", {"start": v(21.5, 3.5) * mm, "end": v(21.5, 1.17) * mm});
            skLineSegment(sketch, "E51", {"start": v(21.5, -1.17) * mm, "end": v(21.5, 1.17) * mm});
            skLineSegment(sketch, "E52", {"start": v(21.5, -1.17) * mm, "end": v(21.5, -3.5) * mm});
            skLineSegment(sketch, "E53", {"start": v(21.5, 1.17) * mm, "end": v(16.5, 1.17) * mm});
            skLineSegment(sketch, "E54", {"start": v(21.5, -1.17) * mm, "end": v(16.5, -1.17) * mm});
            skPoint(sketch, "E55", {"position": v(19, 3.5) * mm});
            skPoint(sketch, "E56", {"position": v(19, -3.5) * mm});
            skLineSegment(sketch, "E57", {"start": v(19, 3.5) * mm, "end": v(19, -3.5) * mm});
            skPoint(sketch, "E58", {"position": v(17.75, 2.25) * mm});
            skLineSegment(sketch, "E59", {"start": v(17.75, 2.25) * mm, "end": v(17.75, 3.5) * mm, "construction": true});
            skLineSegment(sketch, "E60", {"start": v(17.75, 2.25) * mm, "end": v(16.5, 2.25) * mm, "construction": true});
            skLineSegment(sketch, "E61", {"start": v(17.75, 2.25) * mm, "end": v(19, 2.25) * mm, "construction": true});
            skLineSegment(sketch, "E62", {"start": v(17.75, 2.25) * mm, "end": v(17.75, 1.17) * mm, "construction": true});
            skLineSegment(sketch, "E63.bottom", {"start": v(18.07, 2.57) * mm, "end": v(17.43, 2.57) * mm});
            skLineSegment(sketch, "E63.top", {"start": v(18.07, 1.93) * mm, "end": v(17.43, 1.93) * mm});
            skLineSegment(sketch, "E63.left", {"start": v(18.07, 2.57) * mm, "end": v(18.07, 1.93) * mm});
            skLineSegment(sketch, "E63.right", {"start": v(17.43, 2.57) * mm, "end": v(17.43, 1.93) * mm});
            skLineSegment(sketch, "E64.1.0.0", {"start": v(20.57, 2.57) * mm, "end": v(20.57, 1.93) * mm});
            skLineSegment(sketch, "E64.1.0.1", {"start": v(20.57, 2.57) * mm, "end": v(19.93, 2.57) * mm});
            skLineSegment(sketch, "E64.1.0.2", {"start": v(19.93, 2.57) * mm, "end": v(19.93, 1.93) * mm});
            skLineSegment(sketch, "E64.1.0.3", {"start": v(20.57, 1.93) * mm, "end": v(19.93, 1.93) * mm});
            skPoint(sketch, "E65", {"position": v(20.25, 2.25) * mm});
            skLineSegment(sketch, "E66", {"start": v(19, 2.25) * mm, "end": v(20.25, 2.25) * mm, "construction": true});
            skLineSegment(sketch, "E67", {"start": v(20.25, 2.25) * mm, "end": v(21.5, 2.25) * mm, "construction": true});
            skLineSegment(sketch, "E68", {"start": v(20.25, 3.5) * mm, "end": v(20.25, 2.25) * mm, "construction": true});
            skPoint(sketch, "E68.startSnap0", {"position": v(20.25, 2.57) * mm});
            skLineSegment(sketch, "E69", {"start": v(20.25, 1.17) * mm, "end": v(20.25, 2.25) * mm, "construction": true});
            skPoint(sketch, "E70", {"position": v(21.5, 0) * mm});
            skPoint(sketch, "E71.0.1.0", {"position": v(20.25, 0) * mm});
            skLineSegment(sketch, "E71.0.1.1", {"start": v(20.57, 0.32) * mm, "end": v(20.57, -0.32) * mm});
            skLineSegment(sketch, "E71.0.1.2", {"start": v(20.57, 0.32) * mm, "end": v(19.93, 0.32) * mm});
            skLineSegment(sketch, "E71.0.1.3", {"start": v(19.93, 0.32) * mm, "end": v(19.93, -0.32) * mm});
            skLineSegment(sketch, "E71.0.1.4", {"start": v(20.57, -0.32) * mm, "end": v(19.93, -0.32) * mm});
            skLineSegment(sketch, "E71.0.1.5", {"start": v(18.07, 0.32) * mm, "end": v(18.07, -0.32) * mm});
            skLineSegment(sketch, "E71.0.1.6", {"start": v(18.07, -0.32) * mm, "end": v(17.43, -0.32) * mm});
            skLineSegment(sketch, "E71.0.1.7", {"start": v(17.43, 0.32) * mm, "end": v(17.43, -0.32) * mm});
            skLineSegment(sketch, "E71.0.1.8", {"start": v(18.07, 0.32) * mm, "end": v(17.43, 0.32) * mm});
            skPoint(sketch, "E71.0.2.0", {"position": v(20.25, -2.25) * mm});
            skLineSegment(sketch, "E71.0.2.1", {"start": v(20.57, -1.93) * mm, "end": v(20.57, -2.57) * mm});
            skLineSegment(sketch, "E71.0.2.2", {"start": v(20.57, -1.93) * mm, "end": v(19.93, -1.93) * mm});
            skLineSegment(sketch, "E71.0.2.3", {"start": v(19.93, -1.93) * mm, "end": v(19.93, -2.57) * mm});
            skLineSegment(sketch, "E71.0.2.4", {"start": v(20.57, -2.57) * mm, "end": v(19.93, -2.57) * mm});
            skLineSegment(sketch, "E71.0.2.5", {"start": v(18.07, -1.93) * mm, "end": v(18.07, -2.57) * mm});
            skLineSegment(sketch, "E71.0.2.6", {"start": v(18.07, -2.57) * mm, "end": v(17.43, -2.57) * mm});
            skLineSegment(sketch, "E71.0.2.7", {"start": v(17.43, -1.93) * mm, "end": v(17.43, -2.57) * mm});
            skLineSegment(sketch, "E71.0.2.8", {"start": v(18.07, -1.93) * mm, "end": v(17.43, -1.93) * mm});
            skLineSegment(sketch, "E71.direction1", {"start": v(20.25, 2.25) * mm, "end": v(31.55, 2.25) * mm, "construction": true});
            skLineSegment(sketch, "E71.direction2", {"start": v(20.25, 2.25) * mm, "end": v(20.25, 0) * mm, "construction": true});
            skSolve(sketch);
        }
        {
            var Q0;
            Q0=makeQuery(id+"F11.imprint","IMPRINT",FACE,{"disambiguationData":[TD([[makeQuery(id+"F11.imprint","IMPRINT",EDGE,{"derivedFrom":sQuery(id+"F11.wireOp",EDGE,"E71.0.2.1")}),-1.0]])]});
            var Q1;
            Q1=makeQuery(id+"F11.imprint","IMPRINT",FACE,{"disambiguationData":[TD([[makeQuery(id+"F11.imprint","IMPRINT",EDGE,{"derivedFrom":sQuery(id+"F11.wireOp",EDGE,"E71.0.2.5")}),-1.0]])]});
            var Q2;
            Q2=makeQuery(id+"F11.imprint","IMPRINT",FACE,{"disambiguationData":[TD([[makeQuery(id+"F11.imprint","IMPRINT",EDGE,{"derivedFrom":sQuery(id+"F11.wireOp",EDGE,"E71.0.1.5")}),-1.0]])]});
            var Q3;
            Q3=makeQuery(id+"F11.imprint","IMPRINT",FACE,{"disambiguationData":[TD([[makeQuery(id+"F11.imprint","IMPRINT",EDGE,{"derivedFrom":sQuery(id+"F11.wireOp",EDGE,"E71.0.1.1")}),-1.0]])]});
            var Q4;
            Q4=makeQuery(id+"F11.imprint","IMPRINT",FACE,{"disambiguationData":[TD([[makeQuery(id+"F11.imprint","IMPRINT",EDGE,{"derivedFrom":sQuery(id+"F11.wireOp",EDGE,"E64.1.0.0")}),-1.0]])]});
            var Q5;
            Q5=makeQuery(id+"F11.imprint","IMPRINT",FACE,{"disambiguationData":[TD([[makeQuery(id+"F11.imprint","IMPRINT",EDGE,{"derivedFrom":sQuery(id+"F11.wireOp",EDGE,"E63.bottom")}),1.0]])]});
            extrude(context, id + "F12", {"entities" : qUnion([Q0, Q1, Q2, Q3, Q4, Q5]), "operationType" : NewBodyOperationType.ADD, "depth" : 8 * mm});
        }
        {
            var Q0;
            Q0=makeQuery(id+"F3.opExtrude","SWEPT_EDGE",EDGE,{"disambiguationData":[OSD([sQuery(id+"F0.wireOp",EDGE,"E0.left"),sQuery(id+"F0.wireOp",EDGE,"E7.bottom"),sQuery(id+"F0.wireOp",EDGE,"E7.left")])]});
            var Q1;
            Q1=makeQuery(id+"F3.opExtrude","SWEPT_EDGE",EDGE,{"disambiguationData":[OSD([sQuery(id+"F0.wireOp",EDGE,"E7.bottom"),sQuery(id+"F0.wireOp",EDGE,"E7.right")])]});
            var Q2;
            Q2=makeQuery(id+"F3.opExtrude","SWEPT_EDGE",EDGE,{"disambiguationData":[OSD([sQuery(id+"F0.wireOp",EDGE,"E0.left"),sQuery(id+"F0.wireOp",EDGE,"E7.top"),sQuery(id+"F0.wireOp",EDGE,"E7.left")])]});
            var Q3;
            Q3=makeQuery(id+"F3.opExtrude","SWEPT_EDGE",EDGE,{"disambiguationData":[OSD([sQuery(id+"F0.wireOp",EDGE,"E7.top"),sQuery(id+"F0.wireOp",EDGE,"E7.right")])]});
            chamfer(context, id + "F13", {"entities" : qUnion([Q0, Q1, Q2, Q3]), "width" : 0.4 * mm, "tangentPropagation" : true});
        }
        {
            var Q0;
            Q0=qCreatedBy(makeId("Top.planeOp"),FACE);
            cPlane(context, id + "F14", {"entities" : qUnion([Q0]), "cplaneType" : CPlaneType.OFFSET, "offset" : .5 * mm, "oppositeDirection" : true, "width" : 150 * mm, "height" : 150 * mm});
        }
        {
            var Q0;
            Q0=makeQuery(id+"F8.opExtrude","SWEPT_BODY",BODY,{"disambiguationData":[OSD([sQuery(id+"F7.wireOp",EDGE,"E47.0.1.18"),sQuery(id+"F7.wireOp",EDGE,"E47.0.1.19"),sQuery(id+"F7.wireOp",EDGE,"E47.0.1.20"),sQuery(id+"F7.wireOp",EDGE,"E47.0.1.21"),sQuery(id+"F7.wireOp",EDGE,"E47.0.1.22"),sQuery(id+"F7.wireOp",EDGE,"E47.0.1.23"),sQuery(id+"F7.wireOp",EDGE,"E47.0.1.24"),sQuery(id+"F7.wireOp",EDGE,"E47.0.1.25"),sQuery(id+"F7.wireOp",EDGE,"E47.0.1.26"),sQuery(id+"F7.wireOp",EDGE,"E47.0.1.27"),sQuery(id+"F7.wireOp",EDGE,"E47.0.1.28"),sQuery(id+"F7.wireOp",EDGE,"E47.0.1.29"),sQuery(id+"F7.wireOp",EDGE,"E47.0.1.30"),sQuery(id+"F7.wireOp",EDGE,"E47.0.1.31"),sQuery(id+"F7.wireOp",EDGE,"E47.0.1.32"),sQuery(id+"F7.wireOp",EDGE,"E47.0.1.33"),sQuery(id+"F7.wireOp",EDGE,"E47.0.1.34"),sQuery(id+"F7.wireOp",EDGE,"E47.0.1.35"),sQuery(id+"F7.wireOp",EDGE,"E47.0.1.36"),sQuery(id+"F7.wireOp",EDGE,"E47.0.1.37"),sQuery(id+"F7.wireOp",EDGE,"E47.0.1.38"),sQuery(id+"F7.wireOp",EDGE,"E47.0.1.39"),sQuery(id+"F7.wireOp",EDGE,"E47.0.1.40"),sQuery(id+"F7.wireOp",EDGE,"E47.0.1.41"),sQuery(id+"F7.wireOp",EDGE,"E47.0.1.42"),sQuery(id+"F7.wireOp",EDGE,"E47.0.1.43"),sQuery(id+"F7.wireOp",EDGE,"E47.0.1.44"),sQuery(id+"F7.wireOp",EDGE,"E47.0.1.45"),sQuery(id+"F7.wireOp",EDGE,"E47.0.1.46"),sQuery(id+"F7.wireOp",EDGE,"E47.0.1.47"),sQuery(id+"F7.wireOp",EDGE,"E47.0.1.48"),sQuery(id+"F7.wireOp",EDGE,"E47.0.1.49"),sQuery(id+"F7.wireOp",EDGE,"E47.0.1.50"),sQuery(id+"F7.wireOp",EDGE,"E47.0.1.51"),sQuery(id+"F7.wireOp",EDGE,"E47.0.1.52"),sQuery(id+"F7.wireOp",EDGE,"E47.0.1.53"),sQuery(id+"F7.wireOp",EDGE,"E47.0.1.54"),sQuery(id+"F7.wireOp",EDGE,"E47.0.1.55"),sQuery(id+"F7.wireOp",EDGE,"E47.0.1.56"),sQuery(id+"F7.wireOp",EDGE,"E47.0.1.57"),sQuery(id+"F7.wireOp",EDGE,"E47.0.1.58"),sQuery(id+"F7.wireOp",EDGE,"E47.0.1.59"),sQuery(id+"F7.wireOp",EDGE,"E47.0.1.60"),sQuery(id+"F7.wireOp",EDGE,"E47.0.1.61"),sQuery(id+"F7.wireOp",EDGE,"E47.0.1.62"),sQuery(id+"F7.wireOp",EDGE,"E47.0.1.63"),sQuery(id+"F7.wireOp",EDGE,"E47.0.1.64"),sQuery(id+"F7.wireOp",EDGE,"E47.0.1.65"),sQuery(id+"F7.wireOp",EDGE,"E47.0.1.66"),sQuery(id+"F7.wireOp",EDGE,"E47.0.1.67"),sQuery(id+"F7.wireOp",EDGE,"E47.0.1.68"),sQuery(id+"F7.wireOp",EDGE,"E47.0.1.69"),sQuery(id+"F7.wireOp",EDGE,"E47.0.1.70"),sQuery(id+"F7.wireOp",EDGE,"E47.0.1.71"),sQuery(id+"F7.wireOp",EDGE,"E47.0.1.72"),sQuery(id+"F7.wireOp",EDGE,"E47.0.1.73"),sQuery(id+"F7.wireOp",EDGE,"E47.0.1.74"),sQuery(id+"F7.wireOp",EDGE,"E47.0.1.75"),sQuery(id+"F7.wireOp",EDGE,"E47.0.1.76"),sQuery(id+"F7.wireOp",EDGE,"E47.0.1.77"),sQuery(id+"F7.wireOp",EDGE,"E47.0.1.78"),sQuery(id+"F7.wireOp",EDGE,"E47.0.1.79"),sQuery(id+"F7.wireOp",EDGE,"E47.0.1.80"),sQuery(id+"F7.wireOp",EDGE,"E47.0.1.81")])]});
            var Q1;
            Q1=makeQuery(id+"F9.opExtrude","SWEPT_BODY",BODY,{"disambiguationData":[OSD([sQuery(id+"F7.wireOp",EDGE,"E47.0.1.47"),sQuery(id+"F7.wireOp",EDGE,"E47.0.1.75"),sQuery(id+"F7.wireOp",EDGE,"E47.0.1.76"),sQuery(id+"F7.wireOp",EDGE,"E47.0.1.77")])]});
            var Q2;
            Q2=makeQuery(id+"F9.opExtrude","SWEPT_BODY",BODY,{"disambiguationData":[OSD([sQuery(id+"F7.wireOp",EDGE,"E47.0.1.49"),sQuery(id+"F7.wireOp",EDGE,"E47.0.1.52"),sQuery(id+"F7.wireOp",EDGE,"E47.0.1.53"),sQuery(id+"F7.wireOp",EDGE,"E47.0.1.54")])]});
            var Q3;
            Q3=makeQuery(id+"F9.opExtrude","SWEPT_BODY",BODY,{"disambiguationData":[OSD([sQuery(id+"F7.wireOp",EDGE,"E47.0.1.41"),sQuery(id+"F7.wireOp",EDGE,"E47.0.1.58"),sQuery(id+"F7.wireOp",EDGE,"E47.0.1.73"),sQuery(id+"F7.wireOp",EDGE,"E47.0.1.74")])]});
            var Q4;
            Q4=makeQuery(id+"F9.opExtrude","SWEPT_BODY",BODY,{"disambiguationData":[OSD([sQuery(id+"F7.wireOp",EDGE,"E47.0.1.22"),sQuery(id+"F7.wireOp",EDGE,"E47.0.1.23"),sQuery(id+"F7.wireOp",EDGE,"E47.0.1.55"),sQuery(id+"F7.wireOp",EDGE,"E47.0.1.69")])]});
            var Q5;
            Q5=makeQuery(id+"F9.opExtrude","SWEPT_BODY",BODY,{"disambiguationData":[OSD([sQuery(id+"F7.wireOp",EDGE,"E47.0.1.27"),sQuery(id+"F7.wireOp",EDGE,"E47.0.1.33"),sQuery(id+"F7.wireOp",EDGE,"E47.0.1.37"),sQuery(id+"F7.wireOp",EDGE,"E47.0.1.51")])]});
            var Q6;
            Q6=makeQuery(id+"F9.opExtrude","SWEPT_BODY",BODY,{"disambiguationData":[OSD([sQuery(id+"F7.wireOp",EDGE,"E36.3.0.1"),sQuery(id+"F7.wireOp",EDGE,"E36.3.0.2"),sQuery(id+"F7.wireOp",EDGE,"E36.3.0.3"),sQuery(id+"F7.wireOp",EDGE,"E36.3.0.4")])]});
            var Q7;
            Q7=makeQuery(id+"F9.opExtrude","SWEPT_BODY",BODY,{"disambiguationData":[OSD([sQuery(id+"F7.wireOp",EDGE,"E36.2.0.1"),sQuery(id+"F7.wireOp",EDGE,"E36.2.0.2"),sQuery(id+"F7.wireOp",EDGE,"E36.2.0.3"),sQuery(id+"F7.wireOp",EDGE,"E36.2.0.4")])]});
            var Q8;
            Q8=makeQuery(id+"F9.opExtrude","SWEPT_BODY",BODY,{"disambiguationData":[OSD([sQuery(id+"F7.wireOp",EDGE,"E36.1.0.1"),sQuery(id+"F7.wireOp",EDGE,"E36.1.0.2"),sQuery(id+"F7.wireOp",EDGE,"E36.1.0.3"),sQuery(id+"F7.wireOp",EDGE,"E36.1.0.4")])]});
            var Q9;
            Q9=makeQuery(id+"F9.opExtrude","SWEPT_BODY",BODY,{"disambiguationData":[OSD([sQuery(id+"F7.wireOp",EDGE,"E35.bottom"),sQuery(id+"F7.wireOp",EDGE,"E35.top"),sQuery(id+"F7.wireOp",EDGE,"E35.left"),sQuery(id+"F7.wireOp",EDGE,"E35.right")])]});
            var Q10;
            Q10=makeQuery(id+"F9.opExtrude","SWEPT_BODY",BODY,{"disambiguationData":[OSD([sQuery(id+"F7.wireOp",EDGE,"E36.4.0.1"),sQuery(id+"F7.wireOp",EDGE,"E36.4.0.2"),sQuery(id+"F7.wireOp",EDGE,"E36.4.0.3"),sQuery(id+"F7.wireOp",EDGE,"E36.4.0.4")])]});
            var Q11;
            Q11=makeQuery(id+"F9.opExtrude","SWEPT_BODY",BODY,{"disambiguationData":[OSD([sQuery(id+"F7.wireOp",EDGE,"E36.5.0.1"),sQuery(id+"F7.wireOp",EDGE,"E36.5.0.2"),sQuery(id+"F7.wireOp",EDGE,"E36.5.0.3"),sQuery(id+"F7.wireOp",EDGE,"E36.5.0.4")])]});
            var Q12;
            Q12=makeQuery(id+"F9.opExtrude","SWEPT_BODY",BODY,{"disambiguationData":[OSD([sQuery(id+"F7.wireOp",EDGE,"E36.6.0.1"),sQuery(id+"F7.wireOp",EDGE,"E36.6.0.2"),sQuery(id+"F7.wireOp",EDGE,"E36.6.0.3"),sQuery(id+"F7.wireOp",EDGE,"E36.6.0.4")])]});
            var Q13;
            Q13=makeQuery(id+"F9.opExtrude","SWEPT_BODY",BODY,{"disambiguationData":[OSD([sQuery(id+"F7.wireOp",EDGE,"E36.7.0.1"),sQuery(id+"F7.wireOp",EDGE,"E36.7.0.2"),sQuery(id+"F7.wireOp",EDGE,"E36.7.0.3"),sQuery(id+"F7.wireOp",EDGE,"E36.7.0.4")])]});
            var Q14;
            Q14=makeQuery(id+"F9.opExtrude","SWEPT_BODY",BODY,{"disambiguationData":[OSD([sQuery(id+"F7.wireOp",EDGE,"E36.8.0.1"),sQuery(id+"F7.wireOp",EDGE,"E36.8.0.2"),sQuery(id+"F7.wireOp",EDGE,"E36.8.0.3"),sQuery(id+"F7.wireOp",EDGE,"E36.8.0.4")])]});
            var Q15;
            Q15=makeQuery(id+"F9.opExtrude","SWEPT_BODY",BODY,{"disambiguationData":[OSD([sQuery(id+"F7.wireOp",EDGE,"E36.9.0.1"),sQuery(id+"F7.wireOp",EDGE,"E36.9.0.2"),sQuery(id+"F7.wireOp",EDGE,"E36.9.0.3"),sQuery(id+"F7.wireOp",EDGE,"E36.9.0.4")])]});
            var Q16;
            Q16=makeQuery(id+"F9.opExtrude","SWEPT_BODY",BODY,{"disambiguationData":[OSD([sQuery(id+"F7.wireOp",EDGE,"E36.10.0.1"),sQuery(id+"F7.wireOp",EDGE,"E36.10.0.2"),sQuery(id+"F7.wireOp",EDGE,"E36.10.0.3"),sQuery(id+"F7.wireOp",EDGE,"E36.10.0.4")])]});
            var Q17;
            Q17=makeQuery(id+"F9.opExtrude","SWEPT_BODY",BODY,{"disambiguationData":[OSD([sQuery(id+"F7.wireOp",EDGE,"E36.11.0.1"),sQuery(id+"F7.wireOp",EDGE,"E36.11.0.2"),sQuery(id+"F7.wireOp",EDGE,"E36.11.0.3"),sQuery(id+"F7.wireOp",EDGE,"E36.11.0.4")])]});
            var Q18;
            Q18=makeQuery(id+"F9.opExtrude","SWEPT_BODY",BODY,{"disambiguationData":[OSD([sQuery(id+"F7.wireOp",EDGE,"E36.12.0.1"),sQuery(id+"F7.wireOp",EDGE,"E36.12.0.2"),sQuery(id+"F7.wireOp",EDGE,"E36.12.0.3"),sQuery(id+"F7.wireOp",EDGE,"E36.12.0.4")])]});
            var Q19;
            Q19=makeQuery(id+"F9.opExtrude","SWEPT_BODY",BODY,{"disambiguationData":[OSD([sQuery(id+"F7.wireOp",EDGE,"E36.13.0.1"),sQuery(id+"F7.wireOp",EDGE,"E36.13.0.2"),sQuery(id+"F7.wireOp",EDGE,"E36.13.0.3"),sQuery(id+"F7.wireOp",EDGE,"E36.13.0.4")])]});
            var Q20;
            Q20=makeQuery(id+"F9.opExtrude","SWEPT_BODY",BODY,{"disambiguationData":[OSD([sQuery(id+"F7.wireOp",EDGE,"E36.14.0.1"),sQuery(id+"F7.wireOp",EDGE,"E36.14.0.2"),sQuery(id+"F7.wireOp",EDGE,"E36.14.0.3"),sQuery(id+"F7.wireOp",EDGE,"E36.14.0.4")])]});
            var Q21;
            Q21=makeQuery(id+"F9.opExtrude","SWEPT_BODY",BODY,{"disambiguationData":[OSD([sQuery(id+"F7.wireOp",EDGE,"E47.0.1.18"),sQuery(id+"F7.wireOp",EDGE,"E47.0.1.19"),sQuery(id+"F7.wireOp",EDGE,"E47.0.1.20"),sQuery(id+"F7.wireOp",EDGE,"E47.0.1.43")])]});
            var Q22;
            Q22=makeQuery(id+"F9.opExtrude","SWEPT_BODY",BODY,{"disambiguationData":[OSD([sQuery(id+"F7.wireOp",EDGE,"E47.0.1.21"),sQuery(id+"F7.wireOp",EDGE,"E47.0.1.56"),sQuery(id+"F7.wireOp",EDGE,"E47.0.1.60"),sQuery(id+"F7.wireOp",EDGE,"E47.0.1.68")])]});
            var Q23;
            Q23=makeQuery(id+"F9.opExtrude","SWEPT_BODY",BODY,{"disambiguationData":[OSD([sQuery(id+"F7.wireOp",EDGE,"E47.0.1.24"),sQuery(id+"F7.wireOp",EDGE,"E47.0.1.32"),sQuery(id+"F7.wireOp",EDGE,"E47.0.1.40"),sQuery(id+"F7.wireOp",EDGE,"E47.0.1.46")])]});
            var Q24;
            Q24=makeQuery(id+"F9.opExtrude","SWEPT_BODY",BODY,{"disambiguationData":[OSD([sQuery(id+"F7.wireOp",EDGE,"E47.0.1.25"),sQuery(id+"F7.wireOp",EDGE,"E47.0.1.29"),sQuery(id+"F7.wireOp",EDGE,"E47.0.1.44"),sQuery(id+"F7.wireOp",EDGE,"E47.0.1.48")])]});
            var Q25;
            Q25=makeQuery(id+"F9.opExtrude","SWEPT_BODY",BODY,{"disambiguationData":[OSD([sQuery(id+"F7.wireOp",EDGE,"E47.0.1.26"),sQuery(id+"F7.wireOp",EDGE,"E47.0.1.36"),sQuery(id+"F7.wireOp",EDGE,"E47.0.1.63"),sQuery(id+"F7.wireOp",EDGE,"E47.0.1.66")])]});
            var Q26;
            Q26=makeQuery(id+"F9.opExtrude","SWEPT_BODY",BODY,{"disambiguationData":[OSD([sQuery(id+"F7.wireOp",EDGE,"E47.0.1.28"),sQuery(id+"F7.wireOp",EDGE,"E47.0.1.34"),sQuery(id+"F7.wireOp",EDGE,"E47.0.1.42"),sQuery(id+"F7.wireOp",EDGE,"E47.0.1.50")])]});
            var Q27;
            Q27=makeQuery(id+"F9.opExtrude","SWEPT_BODY",BODY,{"disambiguationData":[OSD([sQuery(id+"F7.wireOp",EDGE,"E47.0.1.30"),sQuery(id+"F7.wireOp",EDGE,"E47.0.1.31"),sQuery(id+"F7.wireOp",EDGE,"E47.0.1.35"),sQuery(id+"F7.wireOp",EDGE,"E47.0.1.45")])]});
            var Q28;
            Q28=makeQuery(id+"F9.opExtrude","SWEPT_BODY",BODY,{"disambiguationData":[OSD([sQuery(id+"F7.wireOp",EDGE,"E47.0.1.38"),sQuery(id+"F7.wireOp",EDGE,"E47.0.1.61"),sQuery(id+"F7.wireOp",EDGE,"E47.0.1.64"),sQuery(id+"F7.wireOp",EDGE,"E47.0.1.71")])]});
            var Q29;
            Q29=makeQuery(id+"F9.opExtrude","SWEPT_BODY",BODY,{"disambiguationData":[OSD([sQuery(id+"F7.wireOp",EDGE,"E47.0.1.39"),sQuery(id+"F7.wireOp",EDGE,"E47.0.1.62"),sQuery(id+"F7.wireOp",EDGE,"E47.0.1.65"),sQuery(id+"F7.wireOp",EDGE,"E47.0.1.70")])]});
            var Q30;
            Q30=makeQuery(id+"F9.opExtrude","SWEPT_BODY",BODY,{"disambiguationData":[OSD([sQuery(id+"F7.wireOp",EDGE,"E47.0.1.57"),sQuery(id+"F7.wireOp",EDGE,"E47.0.1.59"),sQuery(id+"F7.wireOp",EDGE,"E47.0.1.67"),sQuery(id+"F7.wireOp",EDGE,"E47.0.1.72")])]});
            var Q31;
            Q31=makeQuery(id+"F8.opExtrude","SWEPT_BODY",BODY,{"disambiguationData":[OSD([sQuery(id+"F7.wireOp",EDGE,"E31.bottom"),sQuery(id+"F7.wireOp",EDGE,"E31.top"),sQuery(id+"F7.wireOp",EDGE,"E31.left"),sQuery(id+"F7.wireOp",EDGE,"E31.right"),sQuery(id+"F7.wireOp",EDGE,"E35.bottom"),sQuery(id+"F7.wireOp",EDGE,"E35.top"),sQuery(id+"F7.wireOp",EDGE,"E35.left"),sQuery(id+"F7.wireOp",EDGE,"E35.right"),sQuery(id+"F7.wireOp",EDGE,"E36.1.0.1"),sQuery(id+"F7.wireOp",EDGE,"E36.1.0.2"),sQuery(id+"F7.wireOp",EDGE,"E36.1.0.3"),sQuery(id+"F7.wireOp",EDGE,"E36.1.0.4"),sQuery(id+"F7.wireOp",EDGE,"E36.2.0.1"),sQuery(id+"F7.wireOp",EDGE,"E36.2.0.2"),sQuery(id+"F7.wireOp",EDGE,"E36.2.0.3"),sQuery(id+"F7.wireOp",EDGE,"E36.2.0.4"),sQuery(id+"F7.wireOp",EDGE,"E36.3.0.1"),sQuery(id+"F7.wireOp",EDGE,"E36.3.0.2"),sQuery(id+"F7.wireOp",EDGE,"E36.3.0.3"),sQuery(id+"F7.wireOp",EDGE,"E36.3.0.4"),sQuery(id+"F7.wireOp",EDGE,"E36.4.0.1"),sQuery(id+"F7.wireOp",EDGE,"E36.4.0.2"),sQuery(id+"F7.wireOp",EDGE,"E36.4.0.3"),sQuery(id+"F7.wireOp",EDGE,"E36.4.0.4"),sQuery(id+"F7.wireOp",EDGE,"E36.5.0.1"),sQuery(id+"F7.wireOp",EDGE,"E36.5.0.2"),sQuery(id+"F7.wireOp",EDGE,"E36.5.0.3"),sQuery(id+"F7.wireOp",EDGE,"E36.5.0.4"),sQuery(id+"F7.wireOp",EDGE,"E36.6.0.1"),sQuery(id+"F7.wireOp",EDGE,"E36.6.0.2"),sQuery(id+"F7.wireOp",EDGE,"E36.6.0.3"),sQuery(id+"F7.wireOp",EDGE,"E36.6.0.4"),sQuery(id+"F7.wireOp",EDGE,"E36.7.0.1"),sQuery(id+"F7.wireOp",EDGE,"E36.7.0.2"),sQuery(id+"F7.wireOp",EDGE,"E36.7.0.3"),sQuery(id+"F7.wireOp",EDGE,"E36.7.0.4"),sQuery(id+"F7.wireOp",EDGE,"E36.8.0.1"),sQuery(id+"F7.wireOp",EDGE,"E36.8.0.2"),sQuery(id+"F7.wireOp",EDGE,"E36.8.0.3"),sQuery(id+"F7.wireOp",EDGE,"E36.8.0.4"),sQuery(id+"F7.wireOp",EDGE,"E36.9.0.1"),sQuery(id+"F7.wireOp",EDGE,"E36.9.0.2"),sQuery(id+"F7.wireOp",EDGE,"E36.9.0.3"),sQuery(id+"F7.wireOp",EDGE,"E36.9.0.4"),sQuery(id+"F7.wireOp",EDGE,"E36.10.0.1"),sQuery(id+"F7.wireOp",EDGE,"E36.10.0.2"),sQuery(id+"F7.wireOp",EDGE,"E36.10.0.3"),sQuery(id+"F7.wireOp",EDGE,"E36.10.0.4"),sQuery(id+"F7.wireOp",EDGE,"E36.11.0.1"),sQuery(id+"F7.wireOp",EDGE,"E36.11.0.2"),sQuery(id+"F7.wireOp",EDGE,"E36.11.0.3"),sQuery(id+"F7.wireOp",EDGE,"E36.11.0.4"),sQuery(id+"F7.wireOp",EDGE,"E36.12.0.1"),sQuery(id+"F7.wireOp",EDGE,"E36.12.0.2"),sQuery(id+"F7.wireOp",EDGE,"E36.12.0.3"),sQuery(id+"F7.wireOp",EDGE,"E36.12.0.4"),sQuery(id+"F7.wireOp",EDGE,"E36.13.0.1"),sQuery(id+"F7.wireOp",EDGE,"E36.13.0.2"),sQuery(id+"F7.wireOp",EDGE,"E36.13.0.3"),sQuery(id+"F7.wireOp",EDGE,"E36.13.0.4"),sQuery(id+"F7.wireOp",EDGE,"E36.14.0.1"),sQuery(id+"F7.wireOp",EDGE,"E36.14.0.2"),sQuery(id+"F7.wireOp",EDGE,"E36.14.0.3"),sQuery(id+"F7.wireOp",EDGE,"E36.14.0.4")])]});
            var Q32;
            Q32=qCreatedBy(id+"F14.planeOp",FACE);
            mirror(context, id + "F15", {"entities" : qUnion([Q0, Q1, Q2, Q3, Q4, Q5, Q6, Q7, Q8, Q9, Q10, Q11, Q12, Q13, Q14, Q15, Q16, Q17, Q18, Q19, Q20, Q21, Q22, Q23, Q24, Q25, Q26, Q27, Q28, Q29, Q30, Q31]), "mirrorPlane" : qUnion([Q32])});
        }
        {
            var Q0;
            Q0=makeQuery(id+"F1.opExtrude","CAP_FACE",FACE,{"disambiguationData":[OSD([sQuery(id+"F0.wireOp",EDGE,"E0.bottom"),sQuery(id+"F0.wireOp",EDGE,"E0.top"),sQuery(id+"F0.wireOp",EDGE,"E0.left"),sQuery(id+"F0.wireOp",EDGE,"E0.right"),sQuery(id+"F0.wireOp",EDGE,"E1"),sQuery(id+"F0.wireOp",EDGE,"E2.0.1.0"),sQuery(id+"F0.wireOp",EDGE,"E2.1.0.0"),sQuery(id+"F0.wireOp",EDGE,"E2.1.1.0"),sQuery(id+"F0.wireOp",EDGE,"E7.left")])],"isStart":false});
            extrude(context, id + "F16", {"entities" : qUnion([Q0]), "operationType" : NewBodyOperationType.REMOVE, "depth" : 25 * mm, "offsetDistance" : 25 * mm});
        }
    });
